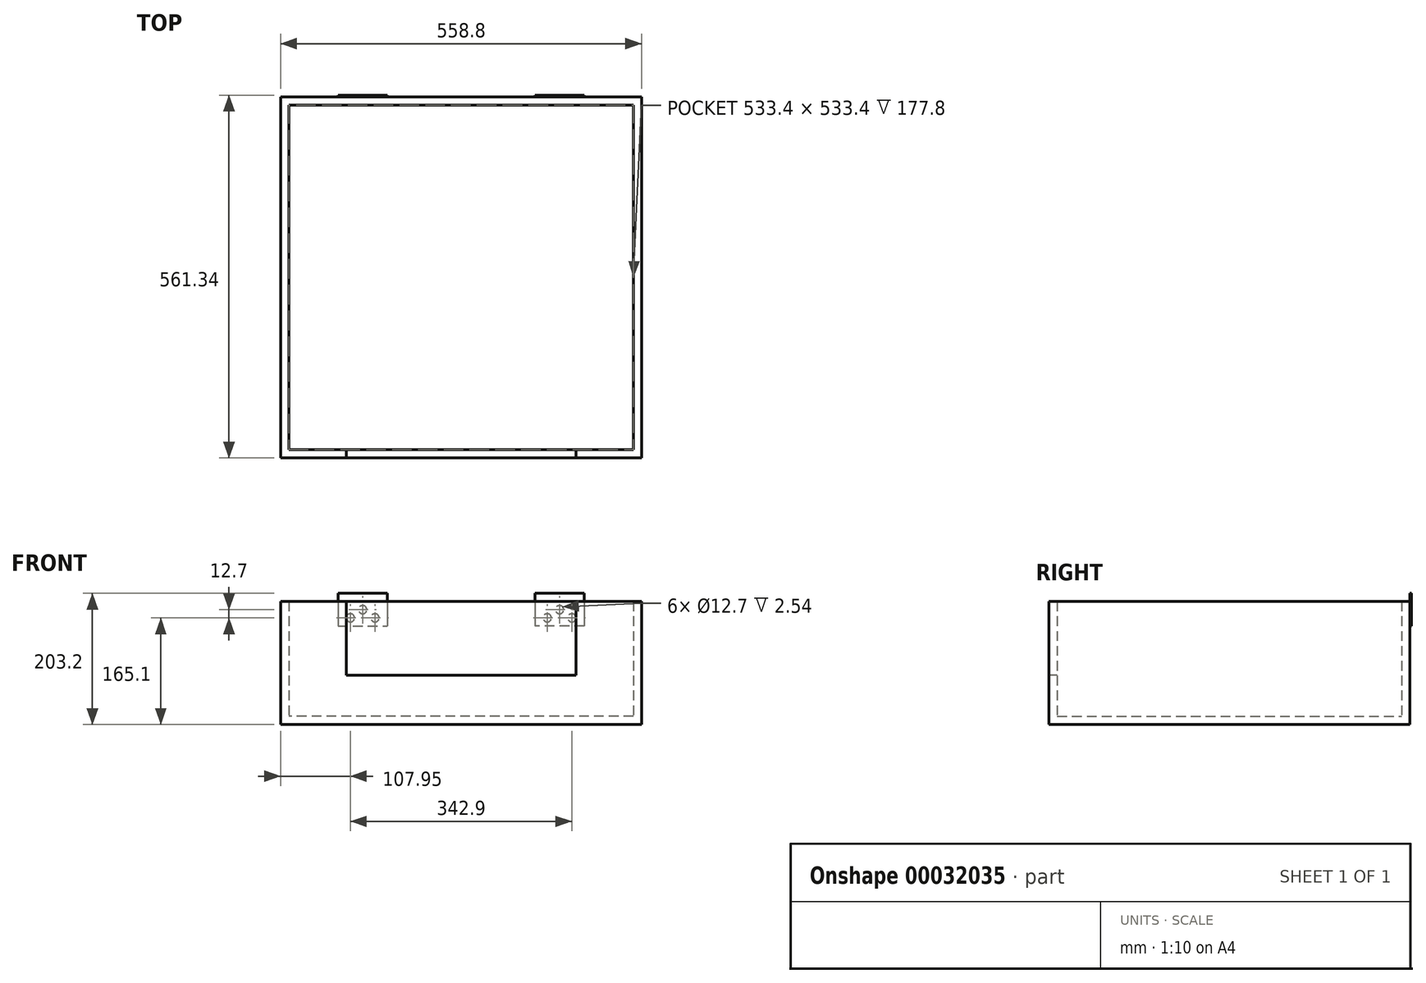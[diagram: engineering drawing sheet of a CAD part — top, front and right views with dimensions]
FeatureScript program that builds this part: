
annotation { "Feature Type Name" : "Feature", "Feature Type Description" : "" }
export const myFeature = defineFeature(function(context is Context, id is Id, definition is map)
    precondition{}
    {
        {
            var Q0;
            Q0=qCreatedBy(makeId("Top.planeOp"),FACE);
            var sketch = newSketch(context, id + "F0", { "sketchPlane" : qUnion([Q0])});
            skLineSegment(sketch, "E0.rect.bottom", {"start": v(279.4, 279.4) * mm, "end": v(-279.4, 279.4) * mm});
            skLineSegment(sketch, "E0.rect.top", {"start": v(279.4, -279.4) * mm, "end": v(-279.4, -279.4) * mm});
            skLineSegment(sketch, "E0.rect.left", {"start": v(279.4, 279.4) * mm, "end": v(279.4, -279.4) * mm});
            skLineSegment(sketch, "E0.rect.right", {"start": v(-279.4, 279.4) * mm, "end": v(-279.4, -279.4) * mm});
            skPoint(sketch, "E0.rect.middle", {"position": v(0, 0) * mm});
            skSolve(sketch);
        }
        {
            var Q0;
            Q0=makeQuery(id+"F0.imprint","IMPRINT",FACE,{"disambiguationData":[TD([[makeQuery(id+"F0.imprint","IMPRINT",EDGE,{"derivedFrom":sQuery(id+"F0.wireOp",EDGE,"E0.rect.bottom")}),1.0]])]});
            extrude(context, id + "F1", {"entities" : qUnion([Q0]), "depth" : 12.7 * mm});
        }
        {
            var Q0;
            Q0=makeQuery(id+"F1.opExtrude","CAP_FACE",FACE,{"disambiguationData":[OSD([sQuery(id+"F0.wireOp",EDGE,"E0.rect.bottom"),sQuery(id+"F0.wireOp",EDGE,"E0.rect.top"),sQuery(id+"F0.wireOp",EDGE,"E0.rect.left"),sQuery(id+"F0.wireOp",EDGE,"E0.rect.right")])],"isStart":false});
            var sketch = newSketch(context, id + "F2", { "sketchPlane" : qUnion([Q0])});
            skLineSegment(sketch, "E1", {"start": v(-279.4, 279.4) * mm, "end": v(-279.4, 266.7) * mm});
            skLineSegment(sketch, "E2.bottom", {"start": v(-279.4, 279.4) * mm, "end": v(279.4, 279.4) * mm});
            skLineSegment(sketch, "E2.top", {"start": v(-279.4, 266.7) * mm, "end": v(279.4, 266.7) * mm});
            skLineSegment(sketch, "E2.right", {"start": v(279.4, 279.4) * mm, "end": v(279.4, 266.7) * mm});
            skLineSegment(sketch, "E3", {"start": v(-279.4, 266.7) * mm, "end": v(-266.7, 266.7) * mm});
            skLineSegment(sketch, "E4.bottom", {"start": v(-279.4, -279.4) * mm, "end": v(-266.7, -279.4) * mm});
            skLineSegment(sketch, "E4.left", {"start": v(-279.4, -279.4) * mm, "end": v(-279.4, 266.7) * mm});
            skLineSegment(sketch, "E4.right", {"start": v(-266.7, -279.4) * mm, "end": v(-266.7, 266.7) * mm});
            skLineSegment(sketch, "E5", {"start": v(279.4, 266.7) * mm, "end": v(266.7, 266.7) * mm});
            skLineSegment(sketch, "E6.bottom", {"start": v(279.4, -279.4) * mm, "end": v(266.7, -279.4) * mm});
            skLineSegment(sketch, "E6.left", {"start": v(279.4, -279.4) * mm, "end": v(279.4, 266.7) * mm});
            skLineSegment(sketch, "E6.right", {"start": v(266.7, -279.4) * mm, "end": v(266.7, 266.7) * mm});
            skSolve(sketch);
        }
        {
            var Q0;
            Q0=makeQuery(id+"F2.imprint","IMPRINT",FACE,{"disambiguationData":[TD([[makeQuery(id+"F2.imprint","IMPRINT",EDGE,{"derivedFrom":sQuery(id+"F2.wireOp",EDGE,"E4.bottom")}),-1.0]])]});
            var Q1;
            Q1=makeQuery(id+"F2.imprint","IMPRINT",FACE,{"disambiguationData":[TD([[makeQuery(id+"F2.imprint","IMPRINT",EDGE,{"derivedFrom":sQuery(id+"F2.wireOp",EDGE,"E2.bottom")}),1.0]])]});
            var Q2;
            Q2=makeQuery(id+"F2.imprint","IMPRINT",FACE,{"disambiguationData":[TD([[makeQuery(id+"F2.imprint","IMPRINT",EDGE,{"derivedFrom":sQuery(id+"F2.wireOp",EDGE,"E6.bottom")}),-1.0]])]});
            extrude(context, id + "F3", {"entities" : qUnion([Q0, Q1, Q2]), "operationType" : NewBodyOperationType.ADD, "depth" : 177.8 * mm});
        }
        {
            var Q0;
            Q0=makeQuery(id+"F1.opExtrude","CAP_FACE",FACE,{"disambiguationData":[OSD([sQuery(id+"F0.wireOp",EDGE,"E0.rect.bottom"),sQuery(id+"F0.wireOp",EDGE,"E0.rect.top"),sQuery(id+"F0.wireOp",EDGE,"E0.rect.left"),sQuery(id+"F0.wireOp",EDGE,"E0.rect.right")])],"isStart":false});
            var sketch = newSketch(context, id + "F4", { "sketchPlane" : qUnion([Q0])});
            skLineSegment(sketch, "E7", {"start": v(-266.7, -279.4) * mm, "end": v(-266.7, -266.7) * mm});
            skLineSegment(sketch, "E8.bottom", {"start": v(266.7, -279.4) * mm, "end": v(-266.7, -279.4) * mm});
            skLineSegment(sketch, "E8.top", {"start": v(266.7, -266.7) * mm, "end": v(-266.7, -266.7) * mm});
            skLineSegment(sketch, "E8.left", {"start": v(266.7, -279.4) * mm, "end": v(266.7, -266.7) * mm});
            skSolve(sketch);
        }
        {
            var Q0;
            Q0=makeQuery(id+"F4.imprint","IMPRINT",FACE,{"disambiguationData":[TD([[makeQuery(id+"F4.imprint","IMPRINT",EDGE,{"derivedFrom":sQuery(id+"F4.wireOp",EDGE,"E8.bottom")}),-1.0]])]});
            extrude(context, id + "F5", {"entities" : qUnion([Q0]), "operationType" : NewBodyOperationType.ADD, "depth" : 63.5 * mm});
        }
        {
            var Q0;
            Q0=makeQuery(id+"F5.opExtrude","CAP_FACE",FACE,{"disambiguationData":[OSD([sQuery(id+"F4.wireOp",EDGE,"E8.bottom"),sQuery(id+"F4.wireOp",EDGE,"E8.top"),sQuery(id+"F4.wireOp",EDGE,"E8.left"),sQuery(id+"F4.wireOp",EDGE,"E7")])],"isStart":false});
            var sketch = newSketch(context, id + "F6", { "sketchPlane" : qUnion([Q0])});
            skLineSegment(sketch, "E9.bottom", {"start": v(-266.7, -266.7) * mm, "end": v(-177.8, -266.7) * mm});
            skLineSegment(sketch, "E9.top", {"start": v(-266.7, -279.4) * mm, "end": v(-177.8, -279.4) * mm});
            skLineSegment(sketch, "E9.left", {"start": v(-266.7, -266.7) * mm, "end": v(-266.7, -279.4) * mm});
            skLineSegment(sketch, "E9.right", {"start": v(-177.8, -266.7) * mm, "end": v(-177.8, -279.4) * mm});
            skLineSegment(sketch, "E10.bottom", {"start": v(266.7, -266.7) * mm, "end": v(177.8, -266.7) * mm});
            skLineSegment(sketch, "E10.top", {"start": v(266.7, -279.4) * mm, "end": v(177.8, -279.4) * mm});
            skLineSegment(sketch, "E10.left", {"start": v(266.7, -266.7) * mm, "end": v(266.7, -279.4) * mm});
            skLineSegment(sketch, "E10.right", {"start": v(177.8, -266.7) * mm, "end": v(177.8, -279.4) * mm});
            skSolve(sketch);
        }
        {
            var Q0;
            Q0=makeQuery(id+"F6.imprint","IMPRINT",FACE,{"disambiguationData":[TD([[makeQuery(id+"F6.imprint","IMPRINT",EDGE,{"derivedFrom":sQuery(id+"F6.wireOp",EDGE,"E9.bottom")}),1.0]])]});
            var Q1;
            Q1=makeQuery(id+"F6.imprint","IMPRINT",FACE,{"disambiguationData":[TD([[makeQuery(id+"F6.imprint","IMPRINT",EDGE,{"derivedFrom":sQuery(id+"F6.wireOp",EDGE,"E10.bottom")}),1.0]])]});
            extrude(context, id + "F7", {"entities" : qUnion([Q0, Q1]), "operationType" : NewBodyOperationType.ADD, "depth" : 114.3 * mm});
        }
        {
            var Q0;
            Q0=makeQuery(id+"F3.boolean.opBoolean","MERGE",FACE,{"derivedFrom":[makeQuery(id+"F1.opExtrude","SWEPT_FACE",FACE,{"disambiguationData":[OSD([sQuery(id+"F0.wireOp",EDGE,"E0.rect.bottom")])]}),makeQuery(id+"F3.opExtrude","SWEPT_FACE",FACE,{"disambiguationData":[OSD([sQuery(id+"F2.wireOp",EDGE,"E2.bottom")])]})]});
            var sketch = newSketch(context, id + "F8", { "sketchPlane" : qUnion([Q0])});
            skLineSegment(sketch, "E11", {"start": v(-279.4, 190.5) * mm, "end": v(-190.5, 190.5) * mm});
            skLineSegment(sketch, "E12", {"start": v(279.4, 190.5) * mm, "end": v(190.5, 190.5) * mm});
            skLineSegment(sketch, "E13.bottom", {"start": v(-190.5, 190.5) * mm, "end": v(-114.3, 190.5) * mm});
            skLineSegment(sketch, "E13.top", {"start": v(-190.5, 152.4) * mm, "end": v(-114.3, 152.4) * mm});
            skLineSegment(sketch, "E13.left", {"start": v(-190.5, 190.5) * mm, "end": v(-190.5, 152.4) * mm});
            skLineSegment(sketch, "E13.right", {"start": v(-114.3, 190.5) * mm, "end": v(-114.3, 152.4) * mm});
            skLineSegment(sketch, "E14.bottom", {"start": v(190.5, 190.5) * mm, "end": v(114.3, 190.5) * mm});
            skLineSegment(sketch, "E14.top", {"start": v(190.5, 152.4) * mm, "end": v(114.3, 152.4) * mm});
            skLineSegment(sketch, "E14.left", {"start": v(190.5, 190.5) * mm, "end": v(190.5, 152.4) * mm});
            skLineSegment(sketch, "E14.right", {"start": v(114.3, 190.5) * mm, "end": v(114.3, 152.4) * mm});
            skSolve(sketch);
        }
        {
            var Q0;
            Q0=makeQuery(id+"F8.imprint","IMPRINT",FACE,{"disambiguationData":[TD([[makeQuery(id+"F8.imprint","IMPRINT",EDGE,{"derivedFrom":sQuery(id+"F8.wireOp",EDGE,"E13.bottom")}),-1.0]])]});
            var Q1;
            Q1=makeQuery(id+"F8.imprint","IMPRINT",FACE,{"disambiguationData":[TD([[makeQuery(id+"F8.imprint","IMPRINT",EDGE,{"derivedFrom":sQuery(id+"F8.wireOp",EDGE,"E14.bottom")}),-1.0]])]});
            extrude(context, id + "F9", {"entities" : qUnion([Q0, Q1]), "operationType" : NewBodyOperationType.ADD, "depth" : 2.54 * mm});
        }
        {
            var Q0;
            Q0=makeQuery(id+"F9.boolean.opBoolean","MERGE",FACE,{"derivedFrom":[makeQuery(id+"F7.boolean.opBoolean","MERGE",FACE,{"derivedFrom":[makeQuery(id+"F3.opExtrude","CAP_FACE",FACE,{"disambiguationData":[OSD([sQuery(id+"F2.wireOp",EDGE,"E2.bottom"),sQuery(id+"F2.wireOp",EDGE,"E2.top"),sQuery(id+"F2.wireOp",EDGE,"E1"),sQuery(id+"F2.wireOp",EDGE,"E2.right"),sQuery(id+"F2.wireOp",EDGE,"E4.bottom"),sQuery(id+"F2.wireOp",EDGE,"E4.left"),sQuery(id+"F2.wireOp",EDGE,"E4.right"),sQuery(id+"F2.wireOp",EDGE,"E6.bottom"),sQuery(id+"F2.wireOp",EDGE,"E6.left"),sQuery(id+"F2.wireOp",EDGE,"E6.right")])],"isStart":false}),makeQuery(id+"F7.opExtrude","CAP_FACE",FACE,{"disambiguationData":[OSD([sQuery(id+"F6.wireOp",EDGE,"E9.bottom"),sQuery(id+"F6.wireOp",EDGE,"E9.top"),sQuery(id+"F6.wireOp",EDGE,"E9.left"),sQuery(id+"F6.wireOp",EDGE,"E9.right")])],"isStart":false}),makeQuery(id+"F7.opExtrude","CAP_FACE",FACE,{"disambiguationData":[OSD([sQuery(id+"F6.wireOp",EDGE,"E10.bottom"),sQuery(id+"F6.wireOp",EDGE,"E10.top"),sQuery(id+"F6.wireOp",EDGE,"E10.left"),sQuery(id+"F6.wireOp",EDGE,"E10.right")])],"isStart":false})]}),makeQuery(id+"F9.opExtrude","SWEPT_FACE",FACE,{"disambiguationData":[OSD([sQuery(id+"F8.wireOp",EDGE,"E13.bottom")])]}),makeQuery(id+"F9.opExtrude","SWEPT_FACE",FACE,{"disambiguationData":[OSD([sQuery(id+"F8.wireOp",EDGE,"E14.bottom")])]})]});
            var sketch = newSketch(context, id + "F10", { "sketchPlane" : qUnion([Q0])});
            skLineSegment(sketch, "E15.bottom", {"start": v(-190.5, 281.94) * mm, "end": v(-114.3, 281.94) * mm});
            skLineSegment(sketch, "E15.top", {"start": v(-190.5, 279.4) * mm, "end": v(-114.3, 279.4) * mm});
            skLineSegment(sketch, "E15.left", {"start": v(-190.5, 281.94) * mm, "end": v(-190.5, 279.4) * mm});
            skLineSegment(sketch, "E15.right", {"start": v(-114.3, 281.94) * mm, "end": v(-114.3, 279.4) * mm});
            skLineSegment(sketch, "E16.bottom", {"start": v(114.3, 281.94) * mm, "end": v(190.5, 281.94) * mm});
            skLineSegment(sketch, "E16.top", {"start": v(114.3, 279.4) * mm, "end": v(190.5, 279.4) * mm});
            skLineSegment(sketch, "E16.left", {"start": v(114.3, 281.94) * mm, "end": v(114.3, 279.4) * mm});
            skLineSegment(sketch, "E16.right", {"start": v(190.5, 281.94) * mm, "end": v(190.5, 279.4) * mm});
            skSolve(sketch);
        }
        {
            var Q0;
            Q0 = qSketchRegion(id + "F10", true);
            extrude(context, id + "F11", {"entities" : qUnion([Q0]), "operationType" : NewBodyOperationType.ADD, "depth" : 12.7 * mm});
        }
        {
            var Q0;
            Q0=makeQuery(id+"F11.boolean.opBoolean","MERGE",FACE,{"derivedFrom":[makeQuery(id+"F9.opExtrude","CAP_FACE",FACE,{"disambiguationData":[OSD([sQuery(id+"F8.wireOp",EDGE,"E13.bottom"),sQuery(id+"F8.wireOp",EDGE,"E13.top"),sQuery(id+"F8.wireOp",EDGE,"E13.left"),sQuery(id+"F8.wireOp",EDGE,"E13.right")])],"isStart":false}),makeQuery(id+"F11.opExtrude","SWEPT_FACE",FACE,{"disambiguationData":[OSD([sQuery(id+"F10.wireOp",EDGE,"E16.bottom")])]})]});
            var sketch = newSketch(context, id + "F12", { "sketchPlane" : qUnion([Q0])});
            skLineSegment(sketch, "E17", {"start": v(-190.5, 177.8) * mm, "end": v(-114.3, 177.8) * mm});
            skLineSegment(sketch, "E18", {"start": v(-152.4, 152.4) * mm, "end": v(-152.4, 203.2) * mm});
            skLineSegment(sketch, "E19", {"start": v(-190.5, 177.8) * mm, "end": v(-152.4, 177.8) * mm});
            skLineSegment(sketch, "E20", {"start": v(-152.4, 177.8) * mm, "end": v(-114.3, 177.8) * mm});
            skLineSegment(sketch, "E21", {"start": v(-152.4, 152.4) * mm, "end": v(-152.4, 177.8) * mm});
            skLineSegment(sketch, "E22", {"start": v(-152.4, 203.2) * mm, "end": v(-152.4, 177.8) * mm});
            skLineSegment(sketch, "E23", {"start": v(-171.45, 177.8) * mm, "end": v(-171.45, 152.4) * mm});
            skLineSegment(sketch, "E24", {"start": v(-133.35, 177.8) * mm, "end": v(-133.35, 152.4) * mm});
            skCircle(sketch, "E25", {"center": v(-152.4, 177.8) * mm, "radius": 6.35 * mm});
            skCircle(sketch, "E26", {"center": v(-171.45, 165.1) * mm, "radius": 6.35 * mm});
            skCircle(sketch, "E27", {"center": v(-133.35, 165.1) * mm, "radius": 6.35 * mm});
            skSolve(sketch);
        }
        {
            var Q0;
            {var subQ0=sQuery(id+"F12.wireOp",EDGE,"E26");var subQ1=sQuery(id+"F12.wireOp",EDGE,"E23");var subQ2=makeQuery(id+"F12.imprint","INTERSECT",VERTEX,{"disambiguationData":[OD(0.0)],"derivedFrom":[subQ1,subQ0]});Q0=makeQuery(id+"F12.imprint","IMPRINT",FACE,{"disambiguationData":[TD([[makeQuery(id+"F12.imprint","IMPRINT",EDGE,{"disambiguationData":[TD([[subQ2,-1.0]])],"derivedFrom":subQ1}),-1.0]])]});}
            var Q1;
            {var subQ0=sQuery(id+"F12.wireOp",EDGE,"E26");var subQ1=sQuery(id+"F12.wireOp",EDGE,"E23");var subQ2=makeQuery(id+"F12.imprint","INTERSECT",VERTEX,{"disambiguationData":[OD(0.0)],"derivedFrom":[subQ1,subQ0]});Q1=makeQuery(id+"F12.imprint","IMPRINT",FACE,{"disambiguationData":[TD([[makeQuery(id+"F12.imprint","IMPRINT",EDGE,{"disambiguationData":[TD([[subQ2,-1.0]])],"derivedFrom":subQ1}),1.0]])]});}
            var Q2;
            {var subQ1=sQuery(id+"F12.wireOp",EDGE,"E19");var subQ3=sQuery(id+"F12.wireOp",EDGE,"E25");var subQ4=makeQuery(id+"F12.imprint","INTERSECT",VERTEX,{"derivedFrom":[subQ1,subQ3]});Q2=makeQuery(id+"F12.imprint","IMPRINT",FACE,{"disambiguationData":[TD([[makeQuery(id+"F12.imprint","IMPRINT",EDGE,{"disambiguationData":[TD([[subQ4,1.0]])],"derivedFrom":subQ3}),1.0]])]});}
            var Q3;
            {var subQ1=sQuery(id+"F12.wireOp",EDGE,"E19");var subQ3=sQuery(id+"F12.wireOp",EDGE,"E25");var subQ4=makeQuery(id+"F12.imprint","INTERSECT",VERTEX,{"derivedFrom":[subQ1,subQ3]});Q3=makeQuery(id+"F12.imprint","IMPRINT",FACE,{"disambiguationData":[TD([[makeQuery(id+"F12.imprint","IMPRINT",EDGE,{"disambiguationData":[TD([[subQ4,-1.0]])],"derivedFrom":subQ3}),1.0]])]});}
            var Q4;
            {var subQ1=sQuery(id+"F12.wireOp",EDGE,"E20");var subQ3=sQuery(id+"F12.wireOp",EDGE,"E25");var subQ4=makeQuery(id+"F12.imprint","INTERSECT",VERTEX,{"derivedFrom":[subQ1,subQ3]});Q4=makeQuery(id+"F12.imprint","IMPRINT",FACE,{"disambiguationData":[TD([[makeQuery(id+"F12.imprint","IMPRINT",EDGE,{"disambiguationData":[TD([[subQ4,1.0]])],"derivedFrom":subQ3}),1.0]])]});}
            var Q5;
            {var subQ1=sQuery(id+"F12.wireOp",EDGE,"E20");var subQ3=sQuery(id+"F12.wireOp",EDGE,"E25");var subQ4=makeQuery(id+"F12.imprint","INTERSECT",VERTEX,{"derivedFrom":[subQ1,subQ3]});Q5=makeQuery(id+"F12.imprint","IMPRINT",FACE,{"disambiguationData":[TD([[makeQuery(id+"F12.imprint","IMPRINT",EDGE,{"disambiguationData":[TD([[subQ4,-1.0]])],"derivedFrom":subQ3}),1.0]])]});}
            var Q6;
            {var subQ0=sQuery(id+"F12.wireOp",EDGE,"E27");var subQ1=sQuery(id+"F12.wireOp",EDGE,"E24");var subQ2=makeQuery(id+"F12.imprint","INTERSECT",VERTEX,{"disambiguationData":[OD(0.0)],"derivedFrom":[subQ1,subQ0]});Q6=makeQuery(id+"F12.imprint","IMPRINT",FACE,{"disambiguationData":[TD([[makeQuery(id+"F12.imprint","IMPRINT",EDGE,{"disambiguationData":[TD([[subQ2,-1.0]])],"derivedFrom":subQ1}),-1.0]])]});}
            var Q7;
            {var subQ0=sQuery(id+"F12.wireOp",EDGE,"E27");var subQ1=sQuery(id+"F12.wireOp",EDGE,"E24");var subQ2=makeQuery(id+"F12.imprint","INTERSECT",VERTEX,{"disambiguationData":[OD(0.0)],"derivedFrom":[subQ1,subQ0]});Q7=makeQuery(id+"F12.imprint","IMPRINT",FACE,{"disambiguationData":[TD([[makeQuery(id+"F12.imprint","IMPRINT",EDGE,{"disambiguationData":[TD([[subQ2,-1.0]])],"derivedFrom":subQ1}),1.0]])]});}
            extrude(context, id + "F13", {"entities" : qUnion([Q0, Q1, Q2, Q3, Q4, Q5, Q6, Q7]), "operationType" : NewBodyOperationType.REMOVE, "oppositeDirection" : true, "depth" : 2.54 * mm});
        }
        {
            var Q0;
            Q0=makeQuery(id+"F11.boolean.opBoolean","MERGE",FACE,{"derivedFrom":[makeQuery(id+"F9.opExtrude","CAP_FACE",FACE,{"disambiguationData":[OSD([sQuery(id+"F8.wireOp",EDGE,"E14.bottom"),sQuery(id+"F8.wireOp",EDGE,"E14.top"),sQuery(id+"F8.wireOp",EDGE,"E14.left"),sQuery(id+"F8.wireOp",EDGE,"E14.right")])],"isStart":false}),makeQuery(id+"F11.opExtrude","SWEPT_FACE",FACE,{"disambiguationData":[OSD([sQuery(id+"F10.wireOp",EDGE,"E15.bottom")])]})]});
            var sketch = newSketch(context, id + "F14", { "sketchPlane" : qUnion([Q0])});
            skLineSegment(sketch, "E28", {"start": v(114.3, 177.8) * mm, "end": v(152.4, 177.8) * mm});
            skPoint(sketch, "E28.endSnap0", {"position": v(152.4, 203.2) * mm});
            skPoint(sketch, "E28.endSnap1", {"position": v(190.5, 177.8) * mm});
            skLineSegment(sketch, "E29", {"start": v(152.4, 177.8) * mm, "end": v(190.5, 177.8) * mm});
            skLineSegment(sketch, "E30", {"start": v(152.4, 203.2) * mm, "end": v(152.4, 177.8) * mm});
            skLineSegment(sketch, "E31", {"start": v(152.4, 152.4) * mm, "end": v(152.4, 177.8) * mm});
            skLineSegment(sketch, "E32", {"start": v(133.35, 177.8) * mm, "end": v(133.35, 152.4) * mm});
            skLineSegment(sketch, "E33", {"start": v(171.45, 177.8) * mm, "end": v(171.45, 152.4) * mm});
            skCircle(sketch, "E34", {"center": v(152.4, 177.8) * mm, "radius": 6.35 * mm});
            skCircle(sketch, "E35", {"center": v(171.45, 165.1) * mm, "radius": 6.35 * mm});
            skCircle(sketch, "E36", {"center": v(133.35, 165.1) * mm, "radius": 6.35 * mm});
            skSolve(sketch);
        }
        {
            var Q0;
            {var subQ1=sQuery(id+"F14.wireOp",EDGE,"E29");var subQ3=sQuery(id+"F14.wireOp",EDGE,"E34");var subQ4=makeQuery(id+"F14.imprint","INTERSECT",VERTEX,{"derivedFrom":[subQ1,subQ3]});Q0=makeQuery(id+"F14.imprint","IMPRINT",FACE,{"disambiguationData":[TD([[makeQuery(id+"F14.imprint","IMPRINT",EDGE,{"disambiguationData":[TD([[subQ4,-1.0]])],"derivedFrom":subQ3}),1.0]])]});}
            var Q1;
            {var subQ1=sQuery(id+"F14.wireOp",EDGE,"E28");var subQ3=sQuery(id+"F14.wireOp",EDGE,"E34");var subQ4=makeQuery(id+"F14.imprint","INTERSECT",VERTEX,{"derivedFrom":[subQ1,subQ3]});Q1=makeQuery(id+"F14.imprint","IMPRINT",FACE,{"disambiguationData":[TD([[makeQuery(id+"F14.imprint","IMPRINT",EDGE,{"disambiguationData":[TD([[subQ4,1.0]])],"derivedFrom":subQ3}),1.0]])]});}
            var Q2;
            {var subQ1=sQuery(id+"F14.wireOp",EDGE,"E28");var subQ3=sQuery(id+"F14.wireOp",EDGE,"E34");var subQ4=makeQuery(id+"F14.imprint","INTERSECT",VERTEX,{"derivedFrom":[subQ1,subQ3]});Q2=makeQuery(id+"F14.imprint","IMPRINT",FACE,{"disambiguationData":[TD([[makeQuery(id+"F14.imprint","IMPRINT",EDGE,{"disambiguationData":[TD([[subQ4,-1.0]])],"derivedFrom":subQ3}),1.0]])]});}
            var Q3;
            {var subQ1=sQuery(id+"F14.wireOp",EDGE,"E29");var subQ3=sQuery(id+"F14.wireOp",EDGE,"E34");var subQ4=makeQuery(id+"F14.imprint","INTERSECT",VERTEX,{"derivedFrom":[subQ1,subQ3]});Q3=makeQuery(id+"F14.imprint","IMPRINT",FACE,{"disambiguationData":[TD([[makeQuery(id+"F14.imprint","IMPRINT",EDGE,{"disambiguationData":[TD([[subQ4,1.0]])],"derivedFrom":subQ3}),1.0]])]});}
            var Q4;
            {var subQ0=sQuery(id+"F14.wireOp",EDGE,"E36");var subQ1=sQuery(id+"F14.wireOp",EDGE,"E32");var subQ2=makeQuery(id+"F14.imprint","INTERSECT",VERTEX,{"disambiguationData":[OD(0.0)],"derivedFrom":[subQ1,subQ0]});Q4=makeQuery(id+"F14.imprint","IMPRINT",FACE,{"disambiguationData":[TD([[makeQuery(id+"F14.imprint","IMPRINT",EDGE,{"disambiguationData":[TD([[subQ2,-1.0]])],"derivedFrom":subQ1}),1.0]])]});}
            var Q5;
            {var subQ0=sQuery(id+"F14.wireOp",EDGE,"E36");var subQ1=sQuery(id+"F14.wireOp",EDGE,"E32");var subQ2=makeQuery(id+"F14.imprint","INTERSECT",VERTEX,{"disambiguationData":[OD(0.0)],"derivedFrom":[subQ1,subQ0]});Q5=makeQuery(id+"F14.imprint","IMPRINT",FACE,{"disambiguationData":[TD([[makeQuery(id+"F14.imprint","IMPRINT",EDGE,{"disambiguationData":[TD([[subQ2,-1.0]])],"derivedFrom":subQ1}),-1.0]])]});}
            var Q6;
            {var subQ0=sQuery(id+"F14.wireOp",EDGE,"E35");var subQ1=sQuery(id+"F14.wireOp",EDGE,"E33");var subQ2=makeQuery(id+"F14.imprint","INTERSECT",VERTEX,{"disambiguationData":[OD(0.0)],"derivedFrom":[subQ1,subQ0]});Q6=makeQuery(id+"F14.imprint","IMPRINT",FACE,{"disambiguationData":[TD([[makeQuery(id+"F14.imprint","IMPRINT",EDGE,{"disambiguationData":[TD([[subQ2,-1.0]])],"derivedFrom":subQ1}),-1.0]])]});}
            var Q7;
            {var subQ0=sQuery(id+"F14.wireOp",EDGE,"E35");var subQ1=sQuery(id+"F14.wireOp",EDGE,"E33");var subQ2=makeQuery(id+"F14.imprint","INTERSECT",VERTEX,{"disambiguationData":[OD(0.0)],"derivedFrom":[subQ1,subQ0]});Q7=makeQuery(id+"F14.imprint","IMPRINT",FACE,{"disambiguationData":[TD([[makeQuery(id+"F14.imprint","IMPRINT",EDGE,{"disambiguationData":[TD([[subQ2,-1.0]])],"derivedFrom":subQ1}),1.0]])]});}
            extrude(context, id + "F15", {"entities" : qUnion([Q0, Q1, Q2, Q3, Q4, Q5, Q6, Q7]), "operationType" : NewBodyOperationType.REMOVE, "oppositeDirection" : true, "depth" : 2.54 * mm});
        }
    });
